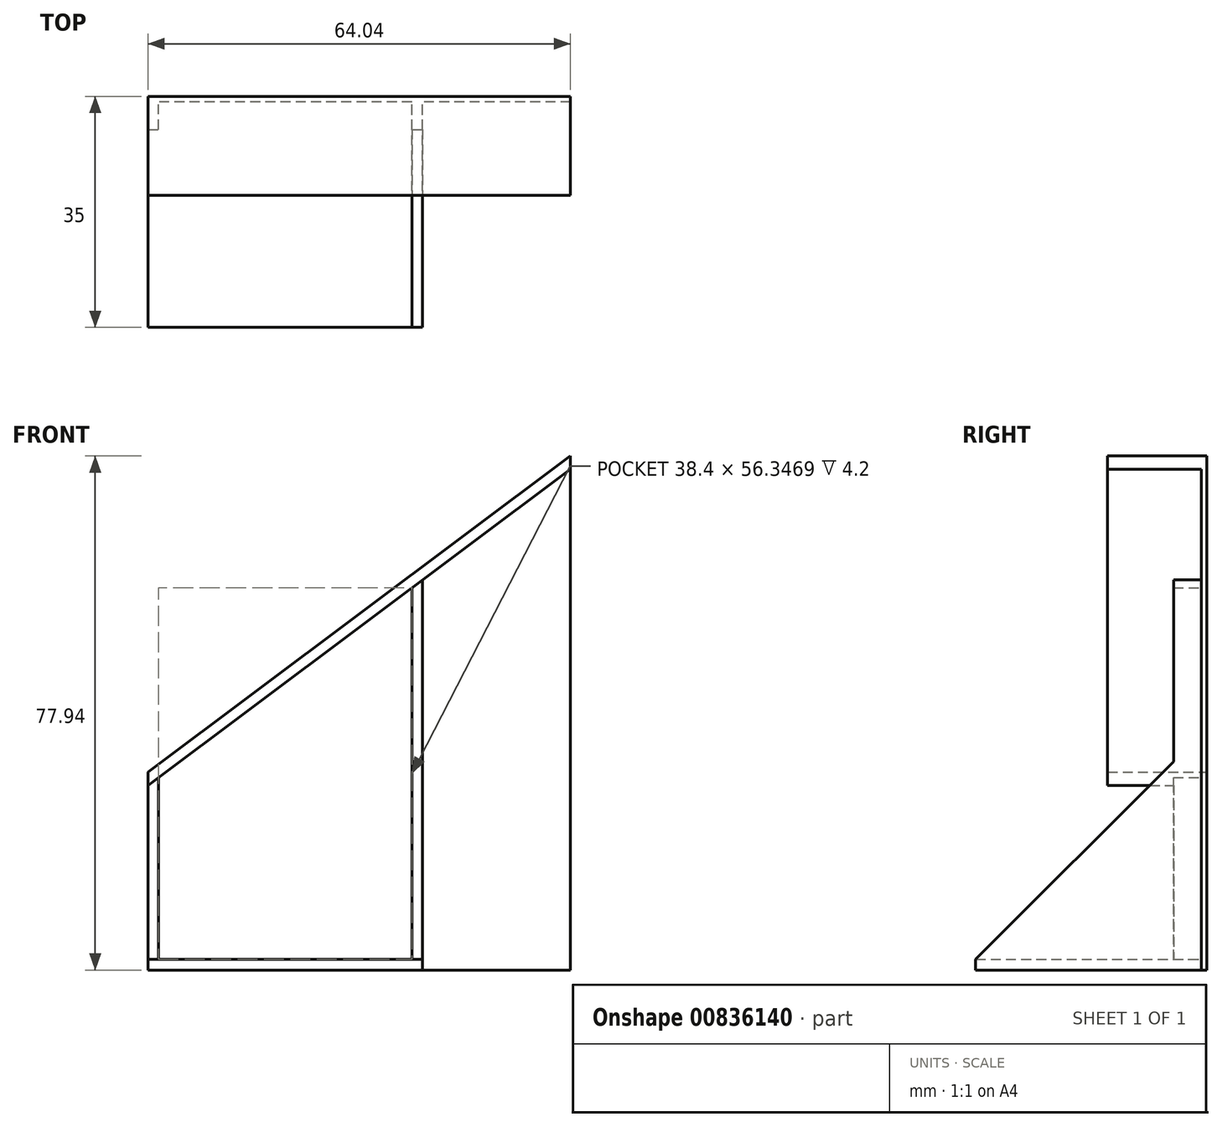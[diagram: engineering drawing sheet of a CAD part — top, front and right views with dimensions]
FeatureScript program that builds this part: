
annotation { "Feature Type Name" : "Feature", "Feature Type Description" : "" }
export const myFeature = defineFeature(function(context is Context, id is Id, definition is map)
    precondition{}
    {
        {
            var Q0;
            Q0=qCreatedBy(makeId("Front.planeOp"),FACE);
            var sketch = newSketch(context, id + "F0", { "sketchPlane" : qUnion([Q0]), "disableImprinting" : false});
            skLineSegment(sketch, "E0", {"start": v(-56.43, 0) * mm, "end": v(92.83, 0) * mm, "construction": true});
            skLineSegment(sketch, "E1", {"start": v(0, 0) * mm, "end": v(64.04, 47.94) * mm});
            skLineSegment(sketch, "E2", {"start": v(0, 0) * mm, "end": v(0, -30) * mm});
            skLineSegment(sketch, "E3", {"start": v(0, -30) * mm, "end": v(64.04, -30) * mm});
            skLineSegment(sketch, "E4", {"start": v(64.04, -30) * mm, "end": v(64.04, 47.94) * mm});
            skLineSegment(sketch, "E5", {"start": v(1.6, -0.8) * mm, "end": v(40, 27.95) * mm});
            skLineSegment(sketch, "E6.bottom", {"start": v(0, -30) * mm, "end": v(40, -30) * mm});
            skLineSegment(sketch, "E6.top", {"start": v(0, -28.4) * mm, "end": v(40, -28.4) * mm});
            skLineSegment(sketch, "E6.left", {"start": v(0, -30) * mm, "end": v(0, -28.4) * mm});
            skLineSegment(sketch, "E6.right", {"start": v(40, -30) * mm, "end": v(40, -28.4) * mm});
            skLineSegment(sketch, "E7", {"start": v(40, -30) * mm, "end": v(40, 27.95) * mm});
            skLineSegment(sketch, "E8", {"start": v(41.6, -30) * mm, "end": v(41.6, 29.14) * mm});
            skLineSegment(sketch, "E9", {"start": v(1.6, -28.4) * mm, "end": v(1.6, -0.8) * mm});
            skLineSegment(sketch, "E10", {"start": v(0, -2) * mm, "end": v(0, 0) * mm});
            skLineSegment(sketch, "E11", {"start": v(64.04, 47.94) * mm, "end": v(64.04, 45.95) * mm});
            skLineSegment(sketch, "E12", {"start": v(40, 27.95) * mm, "end": v(41.6, 29.14) * mm});
            skLineSegment(sketch, "E13", {"start": v(0, -2) * mm, "end": v(1.6, -0.8) * mm});
            skLineSegment(sketch, "E14.trimOffspring", {"start": v(41.6, 29.14) * mm, "end": v(64.04, 45.95) * mm});
            skSolve(sketch);
        }
        {
            var Q0;
            {var subQ0=sQuery(id+"F0.wireOp",EDGE,"E8");var subQ1=makeQuery(id+"F0.imprint","IMPRINT",EDGE,{"derivedFrom":subQ0});var subQ3=sQuery(id+"F0.wireOp",EDGE,"E6.right");var subQ4=makeQuery(id+"F0.imprint","IMPRINT",EDGE,{"derivedFrom":subQ3});var subQ10=sQuery(id+"F0.wireOp",EDGE,"E1");var subQ18=sQuery(id+"F0.wireOp",EDGE,"E9");Q0=qUnion([makeQuery(id+"F0.imprint","IMPRINT",FACE,{"disambiguationData":[TD([[subQ1,-1.0]])]}),makeQuery(id+"F0.imprint","IMPRINT",FACE,{"disambiguationData":[TD([[makeQuery(id+"F0.imprint","IMPRINT",EDGE,{"derivedFrom":subQ18}),1.0]])]}),makeQuery(id+"F0.imprint","IMPRINT",FACE,{"disambiguationData":[TD([[subQ4,1.0]])]}),makeQuery(id+"F0.imprint","IMPRINT",FACE,{"disambiguationData":[TD([[makeQuery(id+"F0.imprint","IMPRINT",EDGE,{"derivedFrom":subQ10}),-1.0]])]}),makeQuery(id+"F0.imprint","IMPRINT",FACE,{"disambiguationData":[TD([[subQ4,-1.0]])]})]);}
            var Q1;
            Q1=makeQuery(id+"F0.imprint","IMPRINT",FACE,{"disambiguationData":[TD([[makeQuery(id+"F0.imprint","IMPRINT",EDGE,{"derivedFrom":sQuery(id+"F0.wireOp",EDGE,"E5")}),-1.0]])]});
            extrude(context, id + "F1", {"entities" : qUnion([Q0, Q1]), "depth" : 0.8 * mm, "offsetDistance" : 25 * mm});
        }
        {
            var Q0;
            {var subQ4=sQuery(id+"F0.wireOp",EDGE,"E6.right");Q0=makeQuery(id+"F0.imprint","IMPRINT",FACE,{"disambiguationData":[TD([[makeQuery(id+"F0.imprint","IMPRINT",EDGE,{"derivedFrom":subQ4}),1.0]])]});}
            extrude(context, id + "F2", {"entities" : qUnion([Q0]), "operationType" : NewBodyOperationType.ADD, "depth" : 35 * mm, "offsetDistance" : 25 * mm});
        }
        {
            var Q0;
            {var subQ1=sQuery(id+"F0.wireOp",EDGE,"E1");Q0=makeQuery(id+"F0.imprint","IMPRINT",FACE,{"disambiguationData":[TD([[makeQuery(id+"F0.imprint","IMPRINT",EDGE,{"derivedFrom":subQ1}),-1.0]])]});}
            extrude(context, id + "F3", {"entities" : qUnion([Q0]), "operationType" : NewBodyOperationType.ADD, "depth" : 15 * mm, "offsetDistance" : 25 * mm});
        }
        {
            var Q0;
            {var subQ1=sQuery(id+"F0.wireOp",EDGE,"E6.right");Q0=makeQuery(id+"F0.imprint","IMPRINT",FACE,{"disambiguationData":[TD([[makeQuery(id+"F0.imprint","IMPRINT",EDGE,{"derivedFrom":subQ1}),-1.0]])]});}
            var Q1;
            {var subQ4=sQuery(id+"F0.wireOp",EDGE,"E9");Q1=makeQuery(id+"F0.imprint","IMPRINT",FACE,{"disambiguationData":[TD([[makeQuery(id+"F0.imprint","IMPRINT",EDGE,{"derivedFrom":subQ4}),1.0]])]});}
            extrude(context, id + "F4", {"entities" : qUnion([Q0, Q1]), "operationType" : NewBodyOperationType.ADD, "depth" : 5 * mm, "offsetDistance" : 25 * mm});
        }
        {
            var Q0;
            Q0=makeQuery(id+"F2.opExtrude","SWEPT_FACE",FACE,{"disambiguationData":[OSD([sQuery(id+"F0.wireOp",EDGE,"E6.right")])]});
            var sketch = newSketch(context, id + "F5", { "sketchPlane" : qUnion([Q0])});
            skLineSegment(sketch, "E15", {"start": v(-35, -28.4) * mm, "end": v(-5, -28.4) * mm});
            skLineSegment(sketch, "E16", {"start": v(-5, -28.4) * mm, "end": v(-5, 1.6) * mm});
            skLineSegment(sketch, "E17", {"start": v(-5, 1.6) * mm, "end": v(-35, -28.4) * mm});
            skLineSegment(sketch, "E18.top", {"start": v(-35, -30) * mm, "end": v(-5, -30) * mm});
            skLineSegment(sketch, "E18.left", {"start": v(-35, -28.4) * mm, "end": v(-35, -30) * mm});
            skLineSegment(sketch, "E18.right", {"start": v(-5, -28.4) * mm, "end": v(-5, -30) * mm});
            skSolve(sketch);
        }
        {
            var Q0;
            Q0=makeQuery(id+"F5.imprint","IMPRINT",FACE,{"disambiguationData":[TD([[makeQuery(id+"F5.imprint","IMPRINT",EDGE,{"derivedFrom":sQuery(id+"F5.wireOp",EDGE,"E15")}),-1.0]])]});
            var Q1;
            Q1=makeQuery(id+"F5.imprint","IMPRINT",FACE,{"disambiguationData":[TD([[makeQuery(id+"F5.imprint","IMPRINT",EDGE,{"derivedFrom":sQuery(id+"F5.wireOp",EDGE,"E16")}),1.0]])]});
            extrude(context, id + "F6", {"entities" : qUnion([Q0, Q1]), "operationType" : NewBodyOperationType.ADD, "depth" : 1.6 * mm, "offsetDistance" : 25 * mm});
        }
    });
